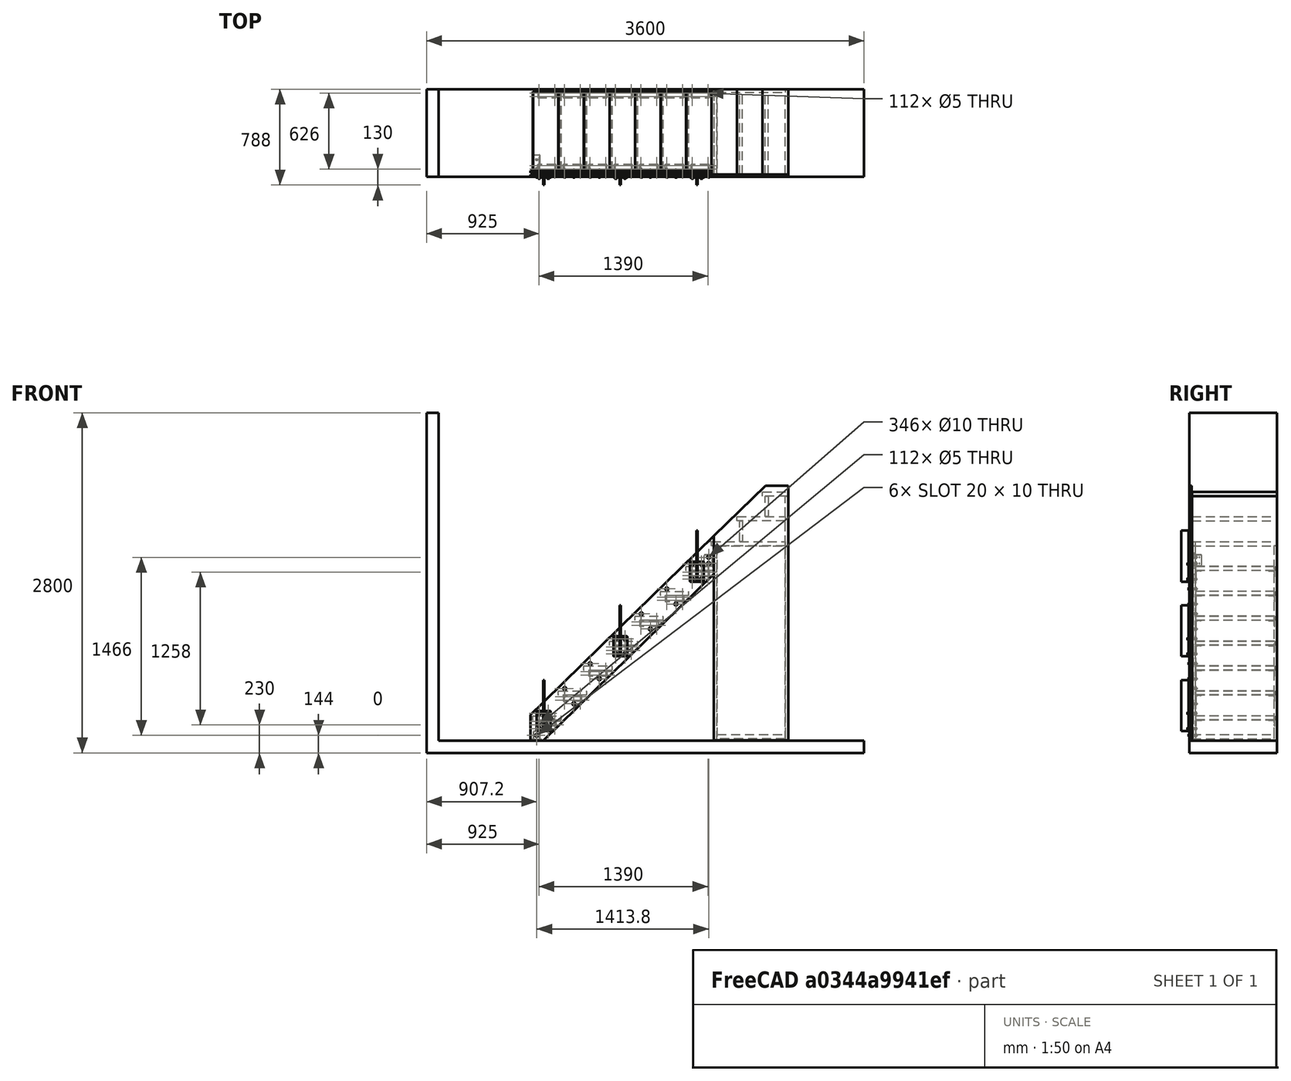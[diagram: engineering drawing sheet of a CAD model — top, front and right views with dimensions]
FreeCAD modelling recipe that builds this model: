
FCSTD DOCUMENT  (FreeCAD 0.17R10980 (Git))
Label: double_beam_board
License: All rights reserved
LicenseURL: http://en.wikipedia.org/wiki/All_rights_reserved
objects: Part::FeaturePython×27, TechDraw::DrawViewDimension×27, Part::Part2DObjectPython×22, TechDraw::DrawViewAnnotation×18, Part::Extrusion×12, Part::Compound×11, Part::Feature×9, TechDraw::DrawViewDetail×7, TechDraw::DrawViewDraft×6, Part::Cut×5, TechDraw::DrawViewPart×3, App::DocumentObjectGroupPython×2, App::DocumentObjectGroup×2, TechDraw::DrawSVGTemplate×1, TechDraw::DrawPage×1
note: 86 computed .brp shape members not serialized (recipe doc carries the construction recipe); baked Part::Feature solids carry a one-line shape summary decoded from their .brp

FEATURE [Part::FeaturePython] beam_01  # a2plus imported part (geometry in sourceFile) (typed FeaturePython)
  fixedPosition = true
  sourceFile = beam.fcstd
  timeLastImport = 1.49397e+09
  updateColors = true
FEATURE [Part::FeaturePython] fridge_box_panels_01  # a2plus imported part (geometry in sourceFile) (typed FeaturePython)
  fixedPosition = false
  sourceFile = A711_fridge_box_panels.fcstd
  timeLastImport = 1.49389e+09
  updateColors = true
FEATURE [Part::Feature] fridge_box_panels_01_cs
  shape: bbox 630 x 3e-07 x 2050 mm, 0 faces, 0 solids (baked)
FEATURE [Part::Part2DObjectPython] DWire  # Draft 2D object (typed FeaturePython)
  ChamferSize = 0
  Closed = true
  End = (1515,-325,1605)
  FilletRadius = 0
  Length = 488.683
  MakeFace = true
  Points = (7) [(1490,-325,1605),(1470,-325,1605),(1470,-325,1640),(1423.45,-325,1640),(1423.45,-325,1757.79),(1515,-325,1757.79),(1515,-325,1605)]
  Start = (1490,-325,1605)
  Subdivisions = 0
  Support = -> [beam_01]
FEATURE [Part::FeaturePython] Clone  label="beam_004"  # Draft clone (typed FeaturePython)
  AttacherType = Attacher::AttachEngine3D
  Objects = -> [beam_01]
  Placement = pos=(0,-30,0) rot=(0,0,1;0rad)
  Scale = (1,1,1)
FEATURE [Part::FeaturePython] stair_profile_01  # a2plus imported part (geometry in sourceFile) (typed FeaturePython)
  fixedPosition = false
  sourceFile = stair_profile.fcstd
  timeLastImport = 1.4938e+09
  updateColors = true
FEATURE [Part::FeaturePython] step_01  # a2plus imported part (geometry in sourceFile) (typed FeaturePython)
  fixedPosition = false
  sourceFile = step.fcstd
  timeLastImport = 1.4938e+09
  updateColors = true
FEATURE [Part::FeaturePython] beam_plate_01  # a2plus imported part (geometry in sourceFile) (typed FeaturePython)
  fixedPosition = false
  sourceFile = beam_plate.fcstd
  timeLastImport = 1.49389e+09
  updateColors = true
FEATURE [Part::Feature] Union
  shape: bbox 26 x 2e-07 x 126 mm, 1 faces, 0 solids (baked)
FEATURE [Part::Feature] Union001
  shape: bbox 86 x 2e-07 x 26 mm, 1 faces, 0 solids (baked)
FEATURE [Part::Part2DObjectPython] Circle001  # Draft 2D object (typed FeaturePython)
  FirstAngle = 0
  LastAngle = 0
  MakeFace = true
  Placement = pos=(32.2,-325,44) rot=(-1,0,0;1.5708rad)
  Radius = 5
FEATURE [Part::Part2DObjectPython] Circle  # Draft 2D object (typed FeaturePython)
  FirstAngle = 0
  LastAngle = 0
  MakeFace = true
  Placement = pos=(1446,-325,1510) rot=(-1,0,0;1.5708rad)
  Radius = 5
FEATURE [Part::Part2DObjectPython] Circle002  # Draft 2D object (typed FeaturePython)
  FirstAngle = 0
  LastAngle = 0
  MakeFace = true
  Placement = pos=(1446,-325,1460) rot=(-1,0,0;1.5708rad)
  Radius = 5
FEATURE [Part::Compound] Compound001
  Links = -> [Union,Union001,DWire]
FEATURE [Part::Compound] Compound002
  Links = -> [Circle001,Circle,Circle002]
FEATURE [Part::Compound] Compound003
  Links = -> [Compound002,Compound001]
FEATURE [Part::Extrusion] Extrude
  Base = -> Compound003
  Dir = (0,-1,0)
  DirMode = 0
  FaceMakerClass = Part::FaceMakerBullseye
  LengthFwd = 20
  LengthRev = 0
  Solid = false
  Symmetric = false
FEATURE [Part::Cut] Cut
  Base = -> beam_01
  Tool = -> Extrude
FEATURE [Part::FeaturePython] Panel001  # WARN: FeaturePython — macro-defined, semantics opaque (R4)
  Area = 0
  Base = -> Cut
  FaceMaker = 0
  HorizontalArea = 0
  Length = 0
  MoveWithHost = false
  Normal = (0,0,0)
  PerimeterLength = 0
  Role = 0
  Sheets = 1
  Thickness = 10
  VerticalArea = 0
  WaveDirection = 0
  WaveHeight = 0
  WaveLength = 0
  WaveType = 0
  Width = 0
FEATURE [Part::Extrusion] Extrude001
  Base = -> Compound002
  Dir = (0,-1,0)
  DirMode = 0
  FaceMakerClass = Part::FaceMakerBullseye
  LengthFwd = 20
  LengthRev = 0
  Placement = pos=(0,-30,0) rot=(0,0,1;0rad)
  Solid = false
  Symmetric = false
FEATURE [Part::Cut] Cut001
  Base = -> Clone
  Tool = -> Extrude001
FEATURE [Part::FeaturePython] Panel  # WARN: FeaturePython — macro-defined, semantics opaque (R4)
  Area = 0
  Base = -> Cut001
  FaceMaker = 0
  HorizontalArea = 0
  Length = 0
  MoveWithHost = false
  Normal = (0,0,0)
  PerimeterLength = 0
  Role = 0
  Sheets = 1
  Thickness = 10
  VerticalArea = 0
  WaveDirection = 0
  WaveHeight = 0
  WaveLength = 0
  WaveType = 0
  Width = 0
FEATURE [Part::Part2DObjectPython] Circle003  # Draft 2D object (typed FeaturePython)
  FirstAngle = 0
  LastAngle = 0
  MakeFace = true
  Placement = pos=(32.2,-375,44) rot=(1,0,0;1.5708rad)
  Radius = 12.5
FEATURE [Part::Extrusion] Extrude002
  Base = -> Circle003
  Dir = (0,-1,0)
  DirMode = 0
  FaceMakerClass = Part::FaceMakerBullseye
  LengthFwd = 2
  LengthRev = 0
  Solid = false
  Symmetric = false
FEATURE [Part::Part2DObjectPython] Circle004  # Draft 2D object (typed FeaturePython)
  FirstAngle = 0
  LastAngle = 0
  MakeFace = true
  Placement = pos=(32.2,-375,44) rot=(1,0,0;1.5708rad)
  Radius = 5
FEATURE [Part::Extrusion] Extrude003
  Base = -> Circle004
  Dir = (0,-1,0)
  DirMode = 0
  FaceMakerClass = Part::FaceMakerBullseye
  LengthFwd = 2
  LengthRev = 0
  Solid = false
  Symmetric = false
FEATURE [Part::Cut] Cut002  label="washer"
  Base = -> Extrude002
  Tool = -> Extrude003
FEATURE [Part::Feature] BOLTS_part011_cs
  Placement = pos=(0,0,-2.5) rot=(0,0,1;0rad)
  shape: bbox 17 x 19.63 x 3e-07 mm, 0 faces, 0 solids (baked)
FEATURE [Part::Extrusion] Extrude004  label="nuts"
  Base = -> BOLTS_part011_cs
  Dir = (0,0,1)
  DirMode = 0
  FaceMakerClass = Part::FaceMakerBullseye
  LengthFwd = 6
  LengthRev = 0
  Placement = pos=(32.2,-347,44) rot=(1,0,0;1.5708rad)
  Solid = true
  Symmetric = false
FEATURE [Part::FeaturePython] Component001  label="washer002"  # WARN: FeaturePython — macro-defined, semantics opaque (R4)
  CloneOf = -> Cut002
  HorizontalArea = 0
  MoveWithHost = false
  PerimeterLength = 0
  Placement = pos=(0,30,0) rot=(0,0,1;0rad)
  Role = 0
  VerticalArea = 0
FEATURE [Part::FeaturePython] Component002  label="washer003"  # WARN: FeaturePython — macro-defined, semantics opaque (R4)
  CloneOf = -> Cut002
  HorizontalArea = 0
  MoveWithHost = false
  PerimeterLength = 0
  Placement = pos=(0,52,0) rot=(0,0,1;0rad)
  Role = 0
  VerticalArea = 0
FEATURE [Part::FeaturePython] Component003  label="nuts001"  # WARN: FeaturePython — macro-defined, semantics opaque (R4)
  CloneOf = -> Extrude004
  HorizontalArea = 0
  MoveWithHost = false
  PerimeterLength = 0
  Placement = pos=(32.2,-317,44) rot=(1,0,0;1.5708rad)
  Role = 0
  VerticalArea = 0
FEATURE [Part::Feature] BOLTS_part  label="Hexagon head bolt DIN 931 M10 - 66.0"
  Placement = pos=(32.2,-383.4,44) rot=(-1,0,0;1.5708rad)
  shape: bbox 17 x 72.4 x 19.63 mm, 11 faces (baked)
FEATURE [TechDraw::DrawSVGTemplate] Template
  EditableTexts = 5cm_scaled_value=50/25/10cm; Architect_2=MARZIA FILATRELLA; Architect_3=MARCO FERRARA; Board_no=A721; Date=5.5.2017; Date_1=5.5.2017; Drawing_title_2=TRAVE PRINCIPALE; Filename=DOUBLE_BEAM.FCSTD; Project_title_2=CASA VACANZE; Project_title_3=A SESTRI; Project_title_4=SCALA INTERNA; Revision=1.0; Scale=VARIE; Sheet_of_sheets=4 DI 7 (nd); Size=A1; Version_1=1.0
  Height = 841
  Orientation = 0
  Width = 594
FEATURE [Part::Feature] step_01_cs  label="hd_steps_cs"
  shape: bbox 1490 x 3e-07 x 1265 mm, 0 faces, 0 solids (baked)
FEATURE [Part::FeaturePython] fridge_box_door_01  # a2plus imported part (geometry in sourceFile) (typed FeaturePython)
  Placement = pos=(0,1e-12,0) rot=(0,0,1;0rad)
  fixedPosition = false
  sourceFile = fridge_box_door.fcstd
  timeLastImport = 1.49385e+09
  updateColors = true
FEATURE [Part::Feature] fridge_box_door_01_cs
  shape: bbox 610 x 3e-07 x 2095 mm, 0 faces, 0 solids (baked)
FEATURE [Part::Part2DObjectPython] DWire003  # Draft 2D object (typed FeaturePython)
  ChamferSize = 0
  Closed = false
  End = (1490,-375,1605)
  FilletRadius = 0
  Length = 55
  MakeFace = true
  Points = (3) [(1470,-375,1640),(1470,-375,1605),(1490,-375,1605)]
  Start = (1470,-375,1640)
  Subdivisions = 0
FEATURE [Part::Part2DObjectPython] Line  # Draft 2D object (typed FeaturePython)
  ChamferSize = 0
  Closed = false
  End = (1490,-375,1640)
  FilletRadius = 0
  Length = 20
  MakeFace = true
  Points = (2) [(1470,-375,1640),(1490,-375,1640)]
  Start = (1470,-375,1640)
  Subdivisions = 0
FEATURE [Part::Part2DObjectPython] Line001  # Draft 2D object (typed FeaturePython)
  ChamferSize = 0
  Closed = false
  End = (1490,-375,0)
  FilletRadius = 0
  Length = 5
  MakeFace = true
  Points = (2) [(1490,-375,5),(1490,-375,0)]
  Start = (1490,-375,5)
  Subdivisions = 0
FEATURE [Part::Part2DObjectPython] Line002  # Draft 2D object (typed FeaturePython)
  ChamferSize = 0
  Closed = false
  End = (2100,-375,0)
  FilletRadius = 0
  Length = 5
  MakeFace = true
  Points = (2) [(2100,-375,5),(2100,-375,2.27374e-13)]
  Start = (2100,-375,5)
  Subdivisions = 0
FEATURE [Part::Part2DObjectPython] DWire001  # Draft 2D object (typed FeaturePython)
  ChamferSize = 0
  Closed = false
  End = (2725,-375,0)
  FilletRadius = 0
  Length = 6200
  MakeFace = true
  Points = (3) [(-775,-375,2700),(-775,-375,-1.13687e-13),(2725,-375,1.00626e-13)]
  Start = (-775,-375,2700)
  Subdivisions = 0
FEATURE [Part::Part2DObjectPython] DWire002  # Draft 2D object (typed FeaturePython)
  ChamferSize = 0
  Closed = false
  End = (2725,-375,2105)
  FilletRadius = 0
  Length = 1405
  MakeFace = true
  Points = (4) [(2725,-375,2260),(2100,-375,2260),(2100,-375,2105),(2725,-375,2105)]
  Start = (2725,-375,2260)
  Subdivisions = 0
FEATURE [Part::Compound] Compound007  label="07_section"
  Links = -> [DWire002,DWire001]
FEATURE [TechDraw::DrawViewDraft] DraftView  label="07_section001"
  Direction = (0,-1,0)
  FontSize = 12
  KeepLabel = false
  LineSpacing = 1
  LineStyle = Solid
  LineWidth = 0.7
  Rotation = -90
  Scale = 0.1
  ScaleType = 2
  Source = -> Compound007
  Symbol = <svg\n xmlns="http://www.w3.org/2000/svg" version="1.1"\n xmlns:freecad="http://www.freecadweb.org/wiki/index.php?title=Svg_Namespace">\n<path id="Compound007_w0000"  d="M -2260.0 -2725.0 L -2260.0 -2100.0 L -2105.0 -2100.0 L -2105.0 -2725.0 " stroke="#000000" stroke-width="7.0 px" style="stroke-width:7.0;stroke-miterlimit:4;stroke-dasharray:none;fill:none;fill-rule: evenodd "/>\n<path id="Compound007_w0001"  d="M -2700.0 775.0 L -5.7e-14 775.0 L -1.01e-13 -2725.0 " stroke="#000000" stroke-width="7.0 px" style="stroke-width:7.0;stroke-miterlimit:4;stroke-dasharray:none;fill:none;fill-rule: evenodd "/>\n\n</svg>
  X = 67.8095
  Y = 363.226
  expr: Y = View.Y + 175.44999999999999
  expr: X = View.X - 136.05000000000001
FEATURE [Part::FeaturePython] Component007  label="07_section002"  # WARN: FeaturePython — macro-defined, semantics opaque (R4)
  CloneOf = -> Compound007
  HorizontalArea = 0
  MoveWithHost = false
  PerimeterLength = 0
  Role = 0
  VerticalArea = 0
FEATURE [Part::FeaturePython] Component008  label="07_section003"  # WARN: FeaturePython — macro-defined, semantics opaque (R4)
  CloneOf = -> Compound007
  HorizontalArea = 0
  MoveWithHost = false
  PerimeterLength = 0
  Role = 0
  VerticalArea = 0
FEATURE [App::DocumentObjectGroupPython] VisGroup001  label="hd_steps"  # scripted group (container) (typed FeaturePython)
  Group = -> [step_01_cs,Component008]
FEATURE [TechDraw::DrawViewDraft] DraftView002  label="hd_steps001"
  Direction = (0,-1,0)
  FontSize = 12
  KeepLabel = false
  LineSpacing = 1
  LineStyle = 3,1
  LineWidth = 0.1
  Rotation = -90
  Scale = 0.1
  ScaleType = 2
  Source = -> VisGroup001
  Symbol = <blob: 2945 chars omitted>
  X = 68.4095
  Y = 363.226
  expr: Y = View.Y + 175.44999999999999
  expr: X = View.X - 135.44999999999999
FEATURE [Part::FeaturePython] Component009  label="07_section004"  # WARN: FeaturePython — macro-defined, semantics opaque (R4)
  CloneOf = -> Compound007
  HorizontalArea = 0
  MoveWithHost = false
  PerimeterLength = 0
  Role = 0
  VerticalArea = 0
FEATURE [Part::FeaturePython] railing_plate_01  # a2plus imported part (geometry in sourceFile) (typed FeaturePython)
  fixedPosition = false
  sourceFile = railing_plate.fcstd
  timeLastImport = 1.49397e+09
  updateColors = true
FEATURE [Part::Compound] Compound010  label="main"
  Links = -> [Panel,Panel001]
FEATURE [Part::Part2DObjectPython] Circle005  # Draft 2D object (typed FeaturePython)
  FirstAngle = 0
  LastAngle = 0
  MakeFace = true
  Placement = pos=(32.2,-375,44) rot=(1,0,0;1.5708rad)
  Radius = 12.5
FEATURE [Part::Extrusion] Extrude007
  Base = -> Circle005
  Dir = (0,-1,0)
  DirMode = 0
  FaceMakerClass = Part::FaceMakerBullseye
  LengthFwd = 2
  LengthRev = 0
  Solid = false
  Symmetric = false
FEATURE [Part::Part2DObjectPython] Circle006  # Draft 2D object (typed FeaturePython)
  FirstAngle = 0
  LastAngle = 0
  MakeFace = true
  Placement = pos=(32.2,-375,44) rot=(1,0,0;1.5708rad)
  Radius = 5
FEATURE [Part::Extrusion] Extrude008
  Base = -> Circle006
  Dir = (0,-1,0)
  DirMode = 0
  FaceMakerClass = Part::FaceMakerBullseye
  LengthFwd = 2
  LengthRev = 0
  Solid = false
  Symmetric = false
FEATURE [Part::Cut] Cut003  label="washer004"
  Base = -> Extrude007
  Placement = pos=(0,-8,0) rot=(0,0,1;0rad)
  Tool = -> Extrude008
FEATURE [Part::Feature] BOLTS_part011_cs001
  Placement = pos=(0,0,-2.5) rot=(0,0,1;0rad)
  shape: bbox 17 x 19.63 x 3e-07 mm, 0 faces, 0 solids (baked)
FEATURE [Part::Extrusion] Extrude009  label="nuts002"
  Base = -> BOLTS_part011_cs001
  Dir = (0,0,1)
  DirMode = 0
  FaceMakerClass = Part::FaceMakerBullseye
  LengthFwd = 6
  LengthRev = 0
  Placement = pos=(32.2,-347,44) rot=(1,0,0;1.5708rad)
  Solid = true
  Symmetric = false
FEATURE [Part::FeaturePython] Component011  label="washer006"  # WARN: FeaturePython — macro-defined, semantics opaque (R4)
  CloneOf = -> Cut003
  HorizontalArea = 0
  MoveWithHost = false
  PerimeterLength = 0
  Placement = pos=(0,30,0) rot=(0,0,1;0rad)
  Role = 0
  VerticalArea = 0
FEATURE [Part::FeaturePython] Component012  label="washer007"  # WARN: FeaturePython — macro-defined, semantics opaque (R4)
  CloneOf = -> Cut003
  HorizontalArea = 0
  MoveWithHost = false
  PerimeterLength = 0
  Placement = pos=(0,52,0) rot=(0,0,1;0rad)
  Role = 0
  VerticalArea = 0
FEATURE [Part::FeaturePython] Component013  label="nuts003"  # WARN: FeaturePython — macro-defined, semantics opaque (R4)
  CloneOf = -> Extrude009
  HorizontalArea = 0
  MoveWithHost = false
  PerimeterLength = 0
  Placement = pos=(32.2,-317,44) rot=(1,0,0;1.5708rad)
  Role = 0
  VerticalArea = 0
FEATURE [Part::Feature] BOLTS_part001  label="Hexagon head bolt DIN 931 M10 - 66.001"
  Placement = pos=(32.2,-391.4,44) rot=(-1,0,0;1.5708rad)
  shape: bbox 17 x 72.4 x 19.63 mm, 11 faces (baked)
FEATURE [Part::Part2DObjectPython] Circle009  # Draft 2D object (typed FeaturePython)
  FirstAngle = 0
  LastAngle = 0
  MakeFace = true
  Placement = pos=(32.2,-355,44) rot=(1,0,0;1.5708rad)
  Radius = 12.5
FEATURE [Part::Extrusion] Extrude013
  Base = -> Circle009
  Dir = (0,1,0)
  DirMode = 0
  FaceMakerClass = Part::FaceMakerBullseye
  LengthFwd = 2
  LengthRev = 0
  Solid = false
  Symmetric = false
FEATURE [Part::Part2DObjectPython] Circle010  # Draft 2D object (typed FeaturePython)
  FirstAngle = 0
  LastAngle = 0
  MakeFace = true
  Placement = pos=(32.2,-355,44) rot=(1,0,0;1.5708rad)
  Radius = 5
FEATURE [Part::Extrusion] Extrude014
  Base = -> Circle010
  Dir = (0,1,0)
  DirMode = 0
  FaceMakerClass = Part::FaceMakerBullseye
  LengthFwd = 2
  LengthRev = 0
  Solid = false
  Symmetric = false
FEATURE [Part::Cut] Cut005  label="washer012"
  Base = -> Extrude013
  Tool = -> Extrude014
FEATURE [Part::Compound] Compound004  label="fastener_and_nuts"
  Links = -> [Cut002,Extrude004,Component003,Component001,Component002,BOLTS_part,Cut005]
FEATURE [Part::FeaturePython] Component005  label="fastener_and_nuts002"  # WARN: FeaturePython — macro-defined, semantics opaque (R4)
  CloneOf = -> Compound004
  HorizontalArea = 0
  MoveWithHost = false
  PerimeterLength = 0
  Placement = pos=(1413.8,0,1466) rot=(0,0,1;0rad)
  Role = 0
  VerticalArea = 0
FEATURE [Part::FeaturePython] Component006  label="fastener_and_nuts003"  # WARN: FeaturePython — macro-defined, semantics opaque (R4)
  CloneOf = -> Compound004
  HorizontalArea = 0
  MoveWithHost = false
  PerimeterLength = 0
  Placement = pos=(1413.8,0,1416) rot=(0,0,1;0rad)
  Role = 0
  VerticalArea = 0
FEATURE [Part::Compound] Compound016  label="fasteners_and_nuts_unique"
  Links = -> [Component005,Compound004,Component006]
FEATURE [Part::FeaturePython] Component  label="washer013"  # WARN: FeaturePython — macro-defined, semantics opaque (R4)
  CloneOf = -> Cut005
  HorizontalArea = 0
  MoveWithHost = false
  PerimeterLength = 0
  Role = 0
  VerticalArea = 0
FEATURE [Part::Compound] Compound013  label="fastener_and_nuts_railing"
  Links = -> [Cut003,Extrude009,Component013,Component011,Component012,BOLTS_part001,Component]
  Placement = pos=(19.6902,0,56) rot=(0,0,1;0rad)
FEATURE [Part::FeaturePython] Component018  label="fastener_and_nuts006"  # WARN: FeaturePython — macro-defined, semantics opaque (R4)
  CloneOf = -> Compound004
  HorizontalArea = 0
  MoveWithHost = false
  PerimeterLength = 0
  Placement = pos=(229.7,0,386) rot=(0,0,1;0rad)
  Role = 0
  VerticalArea = 0
FEATURE [Part::FeaturePython] Array001  # Draft array (typed FeaturePython)
  Angle = 360
  ArrayType = 0
  Axis = (0,0,1)
  Base = -> Component018
  Center = (0,0,0)
  Fuse = false
  IntervalAxis = (0,0,0)
  IntervalX = (75,0,-125)
  IntervalY = (0,0,125)
  IntervalZ = (210,0,205)
  NumberPolar = 1
  NumberX = 2
  NumberY = 1
  NumberZ = 2
FEATURE [Part::FeaturePython] Array002  label="fasteners"  # Draft array (typed FeaturePython)
  Angle = 360
  ArrayType = 0
  Axis = (0,0,1)
  Base = -> Array001
  Center = (0,0,0)
  Fuse = false
  IntervalAxis = (0,0,0)
  IntervalX = (630,0,615)
  IntervalY = (0,1,0)
  IntervalZ = (0,0,0)
  NumberPolar = 1
  NumberX = 2
  NumberY = 1
  NumberZ = 1
FEATURE [Part::FeaturePython] Array  label="fasteners_railing"  # Draft array (typed FeaturePython)
  Angle = 360
  ArrayType = 0
  Axis = (0,0,1)
  Base = -> Compound013
  Center = (0,0,0)
  Fuse = false
  IntervalAxis = (0,0,0)
  IntervalX = (75,0,0)
  IntervalY = (0,0,125)
  IntervalZ = (630,0,615)
  NumberPolar = 1
  NumberX = 2
  NumberY = 2
  NumberZ = 3
FEATURE [Part::Part2DObjectPython] Rectangle  label="gr_detail001"  # Draft 2D object (typed FeaturePython)
  ChamferSize = 0
  Columns = 1
  FilletRadius = 10
  Height = 100
  Length = 100
  MakeFace = false
  Placement = pos=(216.28,-119.156,0) rot=(0,0,1;0rad)
  Rows = 1
FEATURE [TechDraw::DrawViewDraft] DraftView003  label="gr_detailA"
  Direction = (0,0,-1)
  FontSize = 12
  KeepLabel = false
  LineSpacing = 1
  LineStyle = 6,3,.7,3
  LineWidth = 1
  Rotation = 0
  Scale = 0.45
  ScaleType = 2
  Source = -> Rectangle
  Symbol = <svg\n xmlns="http://www.w3.org/2000/svg" version="1.1"\n xmlns:freecad="http://www.freecadweb.org/wiki/index.php?title=Svg_Namespace">\n<path id="Rectangle_w0000"  d="M -226.279953003 119.156494141 L -306.279953003 119.156494141 M -306.279953003 119.156494141 L -316.279953003 109.156494141 L -316.279953003 29.156494141 M -316.279953003 29.156494141 L -306.279953003 19.156494141 L -226.279953003 19.156494141 M -226.279953003 19.156494141 L -216.279953003 29.156494141 L -216.279953003 109.156494141 M -216.279953003 109.156494141 L -226.279953003 119.156494141 " stroke="#000000" stroke-width="2.22222222222 px" style="stroke-width:2.22222222222;stroke-miterlimit:4;stroke-dasharray:13.3333333333,6.66666666667,1.55555555556,6.66666666667;fill:none;fill-rule: evenodd "/>\n\n</svg>
  X = 88.8595
  Y = 87.7759
  expr: Y = front_view.Y - 100
  expr: X = front_view.X - 115
FEATURE [Part::Part2DObjectPython] Rectangle001  # Draft 2D object (typed FeaturePython)
  ChamferSize = 0
  Columns = 1
  FilletRadius = 0
  Height = 1605
  Length = 700
  MakeFace = true
  Placement = pos=(1490,345,0) rot=(0.57735,-0.57735,-0.57735;2.0944rad)
  Rows = 1
  Support = -> [fridge_box_panels_01]
FEATURE [Part::Extrusion] Extrude015  label="fridge_box_side"
  Base = -> Rectangle001
  Dir = (1,0,0)
  DirMode = 0
  FaceMakerClass = Part::FaceMakerBullseye
  LengthFwd = 25
  LengthRev = 0
  Solid = false
  Symmetric = false
FEATURE [Part::Compound] Compound015  label="plan_detail"
  Links = -> [Panel,Panel001,railing_plate_01,beam_plate_01,Array002,Array,Compound016,Extrude015,fridge_box_door_01]
FEATURE [TechDraw::DrawViewPart] View001  label="plan_view"
  ArcCenterMarks = true
  CenterScale = 2
  Direction = (0,0,1)
  HardHidden = false
  HiddenWidth = 0.15
  HorizCenterLine = false
  IsoCount = 0
  IsoHidden = false
  IsoVisible = false
  IsoWidth = 0.3
  KeepLabel = false
  LineWidth = 0.25
  Rotation = 0
  Scale = 0.1
  ScaleType = 2
  SeamHidden = false
  SeamVisible = false
  ShowSectionLine = true
  SmoothHidden = false
  SmoothVisible = false
  Source = -> Compound015
  VertCenterLine = false
  X = -155.002
  Y = 490.968
FEATURE [TechDraw::DrawViewDetail] Detail003  label="DetailA_plan"
  AnchorPoint = (-980,-280,0)
  ArcCenterMarks = true
  BaseView = -> View001
  CenterScale = 2
  Direction = (0,0,1)
  HardHidden = true
  HiddenWidth = 0.15
  HorizCenterLine = false
  IsoCount = 0
  IsoHidden = false
  IsoVisible = false
  IsoWidth = 0.3
  KeepLabel = false
  LineWidth = 0.25
  Radius = 250
  Reference = 1
  Rotation = 0
  Scale = 0.5
  ScaleType = 2
  SeamHidden = false
  SeamVisible = false
  ShowSectionLine = true
  SmoothHidden = false
  SmoothVisible = false
  Source = -> Compound015
  VertCenterLine = false
  X = 166.527
  Y = 442.97
FEATURE [TechDraw::DrawViewDetail] Detail004  label="DetailC_plan"
  AnchorPoint = (375,-280,0)
  ArcCenterMarks = true
  BaseView = -> View001
  CenterScale = 2
  Direction = (0,0,1)
  HardHidden = true
  HiddenWidth = 0.15
  HorizCenterLine = false
  IsoCount = 0
  IsoHidden = false
  IsoVisible = false
  IsoWidth = 0.3
  KeepLabel = false
  LineWidth = 0.25
  Radius = 250
  Reference = 1
  Rotation = 0
  Scale = 0.5
  ScaleType = 2
  SeamHidden = false
  SeamVisible = false
  ShowSectionLine = true
  SmoothHidden = false
  SmoothVisible = false
  Source = -> Compound015
  VertCenterLine = false
  X = 166.527
  Y = 680.166
  expr: X = DetailA_plan.X
FEATURE [TechDraw::DrawViewDraft] DraftView004  label="gr_detailB"
  Direction = (0,0,-1)
  FontSize = 12
  KeepLabel = false
  LineSpacing = 1
  LineStyle = 6,3,.7,3
  LineWidth = 1
  Rotation = 0
  Scale = 0.5
  ScaleType = 2
  Source = -> Rectangle
  Symbol = <svg\n xmlns="http://www.w3.org/2000/svg" version="1.1"\n xmlns:freecad="http://www.freecadweb.org/wiki/index.php?title=Svg_Namespace">\n<path id="Rectangle_w0000"  d="M -226.279953003 119.156494141 L -306.279953003 119.156494141 M -306.279953003 119.156494141 L -316.279953003 109.156494141 L -316.279953003 29.156494141 M -316.279953003 29.156494141 L -306.279953003 19.156494141 L -226.279953003 19.156494141 M -226.279953003 19.156494141 L -216.279953003 29.156494141 L -216.279953003 109.156494141 M -216.279953003 109.156494141 L -226.279953003 119.156494141 " stroke="#000000" stroke-width="2.0 px" style="stroke-width:2.0;stroke-miterlimit:4;stroke-dasharray:12.0,6.0,1.4,6.0;fill:none;fill-rule: evenodd "/>\n\n</svg>
  X = 162.859
  Y = 165.776
  expr: Y = View.Y - 22
  expr: X = View.X - 41
FEATURE [TechDraw::DrawViewDraft] DraftView005  label="gr_detailC"
  Direction = (0,0,-1)
  FontSize = 12
  KeepLabel = false
  LineSpacing = 1
  LineStyle = 6,3,.7,3
  LineWidth = 1
  Rotation = 0
  Scale = 0.5
  ScaleType = 2
  Source = -> Rectangle
  Symbol = <svg\n xmlns="http://www.w3.org/2000/svg" version="1.1"\n xmlns:freecad="http://www.freecadweb.org/wiki/index.php?title=Svg_Namespace">\n<path id="Rectangle_w0000"  d="M -226.279953003 119.156494141 L -306.279953003 119.156494141 M -306.279953003 119.156494141 L -316.279953003 109.156494141 L -316.279953003 29.156494141 M -316.279953003 29.156494141 L -306.279953003 19.156494141 L -226.279953003 19.156494141 M -226.279953003 19.156494141 L -216.279953003 29.156494141 L -216.279953003 109.156494141 M -216.279953003 109.156494141 L -226.279953003 119.156494141 " stroke="#000000" stroke-width="2.0 px" style="stroke-width:2.0;stroke-miterlimit:4;stroke-dasharray:12.0,6.0,1.4,6.0;fill:none;fill-rule: evenodd "/>\n\n</svg>
  X = 217.259
  Y = 226.776
  expr: Y = View.Y + 39
  expr: X = View.X + 13.4
FEATURE [Part::Part2DObjectPython] Shape2DView  label="dr_railing_plate"  # Draft 2D object (typed FeaturePython)
  Base = -> railing_plate_01
  HiddenLines = false
  InPlace = true
  Placement = pos=(0,-375,2.64049e-05) rot=(0.57735,0.57735,-0.57735;2.0944rad)
  Projection = (0,-1,5.9605e-08)
  ProjectionMode = 0
  SegmentLength = 0.05
  Tessellation = false
FEATURE [TechDraw::DrawViewPart] View002  label="axo"
  ArcCenterMarks = true
  CenterScale = 2
  Direction = (-1,1,1)
  HardHidden = true
  HiddenWidth = 0.15
  HorizCenterLine = false
  IsoCount = 0
  IsoHidden = false
  IsoVisible = false
  IsoWidth = 0.3
  KeepLabel = false
  LineWidth = 0.25
  Rotation = 0
  Scale = 0.1
  ScaleType = 2
  SeamHidden = false
  SeamVisible = false
  ShowSectionLine = true
  SmoothHidden = false
  SmoothVisible = false
  Source = -> Compound010
  VertCenterLine = false
  X = -127.92
  Y = 310.072
FEATURE [TechDraw::DrawViewDetail] Detail005  label="DetailA_axo"
  AnchorPoint = (1050,-900,0)
  ArcCenterMarks = true
  BaseView = -> View002
  CenterScale = 2
  Direction = (-1,1,1)
  HardHidden = true
  HiddenWidth = 0.15
  HorizCenterLine = false
  IsoCount = 0
  IsoHidden = false
  IsoVisible = false
  IsoWidth = 0.3
  KeepLabel = false
  LineWidth = 0.25
  Radius = 300
  Reference = 1
  Rotation = 0
  Scale = 0.35
  ScaleType = 2
  SeamHidden = false
  SeamVisible = false
  ShowSectionLine = true
  SmoothHidden = false
  SmoothVisible = false
  Source = -> Compound015
  VertCenterLine = false
  X = 454.166
  Y = 496.192
FEATURE [TechDraw::DrawViewDetail] Detail006  label="DetailC_axo"
  AnchorPoint = (100,800,0)
  ArcCenterMarks = true
  BaseView = -> View002
  CenterScale = 2
  Direction = (-1,1,1)
  HardHidden = true
  HiddenWidth = 0.15
  HorizCenterLine = false
  IsoCount = 0
  IsoHidden = false
  IsoVisible = false
  IsoWidth = 0.3
  KeepLabel = false
  LineWidth = 0.25
  Radius = 300
  Reference = 1
  Rotation = 0
  Scale = 0.35
  ScaleType = 2
  SeamHidden = false
  SeamVisible = false
  ShowSectionLine = true
  SmoothHidden = false
  SmoothVisible = false
  Source = -> Compound015
  VertCenterLine = false
  X = 454.166
  Y = 697.104
  expr: X = DetailA_axo.X
FEATURE [TechDraw::DrawViewAnnotation] Annotation  label="vista_frontale"
  Font = Arial
  KeepLabel = false
  LineSpace = 100
  MaxWidth = -1
  Rotation = 0
  ScaleType = 0
  Text = VISTA FRONTALE | scala 1:10
  TextSize = 3
  TextStyle = 1
  X = 28.6386
  Y = 47.7594
FEATURE [TechDraw::DrawViewAnnotation] Annotation001  label="A"
  Font = Arial
  KeepLabel = false
  LineSpace = 80
  MaxWidth = -1
  Rotation = 0
  ScaleType = 0
  Text = A
  TextSize = 5
  TextStyle = 1
  X = 92.4109
  Y = 83.4178
FEATURE [TechDraw::DrawViewAnnotation] Annotation002  label="B"
  Font = Arial
  KeepLabel = false
  LineSpace = 80
  MaxWidth = -1
  Rotation = 0
  ScaleType = 0
  Text = B
  TextSize = 5
  TextStyle = 1
  X = 167.021
  Y = 162.553
FEATURE [TechDraw::DrawViewAnnotation] Annotation003  label="C"
  Font = Arial
  KeepLabel = false
  LineSpace = 80
  MaxWidth = -1
  Rotation = 0
  ScaleType = 0
  Text = C
  TextSize = 5
  TextStyle = 1
  X = 221.322
  Y = 223.517
FEATURE [TechDraw::DrawViewAnnotation] Annotation004  label="dettaglio_A"
  Font = Arial
  KeepLabel = false
  LineSpace = 100
  MaxWidth = -1
  Rotation = 0
  ScaleType = 0
  Text = DETTAGLIO A |  vista frontale scala 1:5
  TextSize = 3
  TextStyle = 1
  X = 414.908
  Y = 37.4778
  expr: Y = DetailA.Y - 45
  expr: X = DetailA.X - 43
FEATURE [TechDraw::DrawViewAnnotation] Annotation005  label="dettaglio_B"
  Font = Arial
  KeepLabel = false
  LineSpace = 100
  MaxWidth = -1
  Rotation = 0
  ScaleType = 0
  Text = DETTAGLIO B |  vista frontale scala 1:5
  TextSize = 3
  TextStyle = 1
  X = 414.908
  Y = 153.78
  expr: Y = DetailB.Y - 45
  expr: X = DetailB.X - 43
FEATURE [TechDraw::DrawViewAnnotation] Annotation006  label="dettaglio_C"
  Font = Arial
  KeepLabel = false
  LineSpace = 100
  MaxWidth = -1
  Rotation = 0
  ScaleType = 0
  Text = DETTAGLIO C |  vista frontale scala 1:5
  TextSize = 3
  TextStyle = 1
  X = 414.908
  Y = 270.082
  expr: Y = DetailC.Y - 45
  expr: X = DetailC.X - 43
FEATURE [TechDraw::DrawViewAnnotation] Annotation007  label="dettaglio_A_plan"
  Font = Arial
  KeepLabel = false
  LineSpace = 100
  MaxWidth = -1
  Rotation = 0
  ScaleType = 0
  Text = DETTAGLIO A |  pianta scala 1:2
  TextSize = 3
  TextStyle = 1
  X = 78.0268
  Y = 351.67
  expr: Y = DetailA_plan.Y - 91.299999999999997
  expr: X = DetailA_plan.X - 88.5
FEATURE [TechDraw::DrawViewAnnotation] Annotation008  label="dettaglio_C_plan"
  Font = Arial
  KeepLabel = false
  LineSpace = 100
  MaxWidth = -1
  Rotation = 0
  ScaleType = 0
  Text = DETTAGLIO C |  pianta scala 1:2
  TextSize = 3
  TextStyle = 1
  X = 78.0268
  Y = 588.866
  expr: Y = DetailC_plan.Y - 91.299999999999997
  expr: X = DetailC_plan.X - 88.5
FEATURE [TechDraw::DrawViewAnnotation] Annotation009  label="dettaglio_A_axo"
  Font = Arial
  KeepLabel = false
  LineSpace = 100
  MaxWidth = -1
  Rotation = 0
  ScaleType = 0
  Text = DETTAGLIO A | vista assonometrica
  TextSize = 3
  TextStyle = 1
  X = 379.866
  Y = 418.692
  expr: Y = DetailA_axo.Y - 77.5
  expr: X = DetailA_axo.X - 74.299999999999997
FEATURE [TechDraw::DrawViewAnnotation] Annotation010  label="dettaglio_C_axo"
  Font = Arial
  KeepLabel = false
  LineSpace = 100
  MaxWidth = -1
  Rotation = 0
  ScaleType = 0
  Text = DETTAGLIO C | vista assonometrica
  TextSize = 3
  TextStyle = 1
  X = 379.866
  Y = 619.604
  expr: Y = DetailC_axo.Y - 77.5
  expr: X = DetailC_axo.X - 74.299999999999997
FEATURE [TechDraw::DrawViewDimension] Dimension025
  Font = Arial
  Fontsize = 3
  FormatSpec = %value%
  KeepLabel = false
  LineWidth = 0.1
  MeasureType = 1
  References2D = -> [Detail003]
  Rotation = 0
  ScaleType = 0
  Type = 2
  X = -50.2948
  Y = 3.01167
FEATURE [TechDraw::DrawViewDimension] Dimension026
  Font = Arial
  Fontsize = 3
  FormatSpec = %value%
  KeepLabel = false
  LineWidth = 0.1
  MeasureType = 1
  References2D = -> [Detail003]
  Rotation = 0
  ScaleType = 0
  Type = 2
  X = -49.4415
  Y = 15.8113
FEATURE [TechDraw::DrawViewDimension] Dimension027
  Font = Arial
  Fontsize = 3
  FormatSpec = %value%
  KeepLabel = false
  LineWidth = 0.1
  MeasureType = 1
  References2D = -> [Detail003]
  Rotation = 0
  ScaleType = 0
  Type = 2
  X = -58.7275
  Y = 10.2899
FEATURE [TechDraw::DrawViewDimension] Dimension028
  Font = Arial
  Fontsize = 3
  FormatSpec = Distanziatore da 1cm
  KeepLabel = false
  LineWidth = 0.1
  MeasureType = 1
  References2D = -> [Detail003]
  Rotation = 0
  ScaleType = 0
  Type = 2
  X = 44.5465
  Y = -27.1287
FEATURE [Part::FeaturePython] plate_01  # a2plus imported part (geometry in sourceFile) (typed FeaturePython)
  fixedPosition = false
  sourceFile = plate.fcstd
  timeLastImport = 1.49399e+09
  updateColors = true
FEATURE [Part::Compound] Compound  label="main_view"
  Links = -> [Panel,Panel001,Component009,plate_01]
FEATURE [App::DocumentObjectGroup] Group  label="utilities"
  Group = -> [step_01,stair_profile_01,fridge_box_panels_01_cs,fridge_box_panels_01,beam_plate_01,fridge_box_door_01,plate_01]
FEATURE [TechDraw::DrawViewPart] View  label="front_view"
  ArcCenterMarks = true
  CenterScale = 2.5
  Direction = (0,-1,0)
  HardHidden = true
  HiddenWidth = 0.1
  HorizCenterLine = false
  IsoCount = 0
  IsoHidden = false
  IsoVisible = false
  IsoWidth = 0.3
  KeepLabel = false
  LineWidth = 0.25
  Rotation = 0
  Scale = 0.1
  ScaleType = 2
  SeamHidden = false
  SeamVisible = false
  ShowSectionLine = true
  SmoothHidden = false
  SmoothVisible = false
  Source = -> Compound
  VertCenterLine = false
  X = 203.859
  Y = 187.776
FEATURE [Part::Part2DObjectPython] DWire004  # Draft 2D object (typed FeaturePython)
  ChamferSize = 0
  Closed = true
  End = (-875,-375,2700)
  FilletRadius = 0
  Length = 12800
  MakeFace = true
  Points = (6) [(-775,-375,2700),(-775,-375,-2.27374e-13),(2725,-375,2.27374e-13),(2725,-375,-100),(-875,-375,-100),(-875,-375,2700)]
  Start = (-775,-375,2700)
  Subdivisions = 0
  Support = -> [Compound]
FEATURE [Part::Extrusion] Extrude006  label="floor"
  Base = -> DWire004
  Dir = (0,1,0)
  DirMode = 0
  FaceMakerClass = Part::FaceMakerBullseye
  LengthFwd = 720
  LengthRev = 0
  Solid = false
  Symmetric = false
FEATURE [Part::Compound] Compound008  label="details"
  Links = -> [Panel,Panel001,fridge_box_panels_01,beam_plate_01,Extrude006,step_01,fridge_box_door_01,railing_plate_01,plate_01]
FEATURE [TechDraw::DrawViewDetail] Detail  label="DetailA"
  AnchorPoint = (-900,-1150,0)
  ArcCenterMarks = true
  BaseView = -> View
  CenterScale = 2.5
  Direction = (0,-1,0)
  HardHidden = true
  HiddenWidth = 0.15
  HorizCenterLine = false
  IsoCount = 0
  IsoHidden = false
  IsoVisible = false
  IsoWidth = 0.3
  KeepLabel = false
  LineWidth = 0.25
  Radius = 300
  Reference = 1
  Rotation = 0
  Scale = 0.2
  ScaleType = 2
  SeamHidden = false
  SeamVisible = false
  ShowSectionLine = true
  SmoothHidden = false
  SmoothVisible = false
  Source = -> Compound008
  VertCenterLine = false
  X = 457.908
  Y = 82.4778
  expr: AnchorPoint.y = 250 - Compound008.Shape.BoundBox.ZLength / 2
  expr: AnchorPoint.x = 900 - Compound008.Shape.BoundBox.XLength / 2
FEATURE [TechDraw::DrawViewDetail] Detail001  label="DetailC"
  AnchorPoint = (500,200,0)
  ArcCenterMarks = true
  BaseView = -> View
  CenterScale = 2.5
  Direction = (0,-1,0)
  HardHidden = true
  HiddenWidth = 0.15
  HorizCenterLine = false
  IsoCount = 0
  IsoHidden = false
  IsoVisible = false
  IsoWidth = 0.3
  KeepLabel = false
  LineWidth = 0.25
  Radius = 300
  Reference = 1
  Rotation = 0
  Scale = 0.2
  ScaleType = 2
  SeamHidden = false
  SeamVisible = false
  ShowSectionLine = true
  SmoothHidden = false
  SmoothVisible = false
  Source = -> Compound008
  VertCenterLine = false
  X = 457.908
  Y = 315.082
  expr: X = DetailA.X
  expr: AnchorPoint.y = 1600 - Compound008.Shape.BoundBox.ZLength / 2
  expr: AnchorPoint.x = 2300 - Compound008.Shape.BoundBox.XLength / 2
FEATURE [TechDraw::DrawViewDetail] Detail002  label="DetailB"
  AnchorPoint = (-100,-425,0)
  ArcCenterMarks = true
  BaseView = -> View
  CenterScale = 2.5
  Direction = (0,-1,0)
  HardHidden = true
  HiddenWidth = 0.15
  HorizCenterLine = false
  IsoCount = 0
  IsoHidden = false
  IsoVisible = false
  IsoWidth = 0.3
  KeepLabel = false
  LineWidth = 0.25
  Radius = 300
  Reference = 1
  Rotation = 0
  Scale = 0.2
  ScaleType = 2
  SeamHidden = false
  SeamVisible = false
  ShowSectionLine = true
  SmoothHidden = false
  SmoothVisible = false
  Source = -> Compound008
  VertCenterLine = false
  X = 457.908
  Y = 198.78
  expr: AnchorPoint.y = 50 + Detail.AnchorPoint.y + (Detail001.AnchorPoint.y - Detail.AnchorPoint.y) / 2
  expr: AnchorPoint.x = 100 + Detail.AnchorPoint.x + (Detail001.AnchorPoint.x - Detail.AnchorPoint.x) / 2
  expr: X = Detail.X
  expr: Y = Detail.Y + (Detail001.Y - Detail.Y) / 2
FEATURE [TechDraw::DrawViewDimension] Dimension
  Font = Arial
  Fontsize = 3
  FormatSpec = %value%
  KeepLabel = false
  LineWidth = 0.1
  MeasureType = 1
  References2D = -> [View]
  Rotation = 0
  ScaleType = 0
  Type = 1
  X = -29.5609
  Y = 154.149
FEATURE [TechDraw::DrawViewDimension] Dimension001
  Font = Arial
  Fontsize = 3
  FormatSpec = %value%
  KeepLabel = false
  LineWidth = 0.1
  MeasureType = 1
  References2D = -> [View]
  Rotation = 0
  ScaleType = 0
  Type = 2
  X = 67.4529
  Y = 30.762
FEATURE [TechDraw::DrawViewDimension] Dimension002
  Font = Arial
  Fontsize = 3
  FormatSpec = %value%
  KeepLabel = false
  LineWidth = 0.1
  MeasureType = 1
  References2D = -> [View]
  Rotation = 0
  ScaleType = 0
  Type = 0
  X = -56.5427
  Y = 88.758
FEATURE [TechDraw::DrawViewDimension] Dimension003
  Font = Arial
  Fontsize = 3
  FormatSpec = %value%
  KeepLabel = false
  LineWidth = 0.1
  MeasureType = 1
  References2D = -> [View]
  Rotation = 0
  ScaleType = 0
  Type = 0
  X = -52.3631
  Y = 57.1395
FEATURE [TechDraw::DrawViewDimension] Dimension004
  Font = Arial
  Fontsize = 3
  FormatSpec = %value%
  KeepLabel = false
  LineWidth = 0.1
  MeasureType = 1
  References2D = -> [View]
  Rotation = 0
  ScaleType = 0
  Type = 0
  X = -26.6032
  Y = 84.8777
FEATURE [TechDraw::DrawViewDimension] Dimension005
  Font = Arial
  Fontsize = 3
  FormatSpec = %value%
  KeepLabel = false
  LineWidth = 0.1
  MeasureType = 1
  References2D = -> [View]
  Rotation = 0
  ScaleType = 0
  Type = 2
  X = 56.7794
  Y = -18.033
FEATURE [TechDraw::DrawViewDimension] Dimension006
  Font = Arial
  Fontsize = 3
  FormatSpec = %value%
  KeepLabel = false
  LineWidth = 0.1
  MeasureType = 1
  References2D = -> [View]
  Rotation = 0
  ScaleType = 0
  Type = 1
  X = -106.571
  Y = 139.599
FEATURE [TechDraw::DrawViewDimension] Dimension007
  Font = Arial
  Fontsize = 3
  FormatSpec = %value%
  KeepLabel = false
  LineWidth = 0.1
  MeasureType = 1
  References2D = -> [View]
  Rotation = 0
  ScaleType = 0
  Type = 2
  X = -108.326
  Y = 123.557
FEATURE [TechDraw::DrawViewDimension] Dimension008
  Font = Arial
  Fontsize = 3
  FormatSpec = %value%
  KeepLabel = false
  LineWidth = 0.1
  MeasureType = 1
  References2D = -> [Detail]
  Rotation = 0
  ScaleType = 0
  Type = 2
  X = -20.5658
  Y = 7.14574
FEATURE [TechDraw::DrawViewDimension] Dimension009
  Font = Arial
  Fontsize = 3
  FormatSpec = %value%
  KeepLabel = false
  LineWidth = 0.1
  MeasureType = 1
  References2D = -> [Detail]
  Rotation = 0
  ScaleType = 0
  Type = 1
  X = 1.39429
  Y = 34.1601
FEATURE [TechDraw::DrawViewDimension] Dimension012
  Font = Arial
  Fontsize = 3
  FormatSpec = %value%
  KeepLabel = false
  LineWidth = 0.1
  MeasureType = 1
  References2D = -> [Detail]
  Rotation = 0
  ScaleType = 0
  Type = 1
  X = -14.8143
  Y = -18.8229
FEATURE [TechDraw::DrawViewDimension] Dimension013
  Font = Arial
  Fontsize = 3
  FormatSpec = %value%
  KeepLabel = false
  LineWidth = 0.1
  MeasureType = 1
  References2D = -> [Detail]
  Rotation = 0
  ScaleType = 0
  Type = 2
  X = 29.6067
  Y = -3.10529
FEATURE [TechDraw::DrawViewDimension] Dimension014
  Font = Arial
  Fontsize = 3
  FormatSpec = %value%
  KeepLabel = false
  LineWidth = 0.1
  MeasureType = 1
  References2D = -> [Detail]
  Rotation = 0
  ScaleType = 0
  Type = 1
  X = 12.6289
  Y = 16.3443
FEATURE [TechDraw::DrawViewDimension] Dimension015
  Font = Arial
  Fontsize = 3
  FormatSpec = %value%
  KeepLabel = false
  LineWidth = 0.1
  MeasureType = 1
  References2D = -> [Detail002]
  Rotation = 0
  ScaleType = 0
  Type = 2
  X = -5.15487
  Y = -0.381842
FEATURE [TechDraw::DrawViewDimension] Dimension016
  Font = Arial
  Fontsize = 3
  FormatSpec = %value%
  KeepLabel = false
  LineWidth = 0.1
  MeasureType = 1
  References2D = -> [Detail002]
  Rotation = 0
  ScaleType = 0
  Type = 1
  X = -21.1922
  Y = 38.1842
FEATURE [TechDraw::DrawViewDimension] Dimension017
  Font = Arial
  Fontsize = 3
  FormatSpec = %value%
  KeepLabel = false
  LineWidth = 0.1
  MeasureType = 1
  References2D = -> [Detail002]
  Rotation = 0
  ScaleType = 0
  Type = 1
  X = -32.6475
  Y = 38.1842
FEATURE [TechDraw::DrawViewDimension] Dimension018
  Font = Arial
  Fontsize = 3
  FormatSpec = %value%
  KeepLabel = false
  LineWidth = 0.1
  MeasureType = 1
  References2D = -> [Detail002]
  Rotation = 0
  ScaleType = 0
  Type = 1
  X = 0
  Y = 38.1842
FEATURE [TechDraw::DrawViewDimension] Dimension019
  Font = Arial
  Fontsize = 3
  FormatSpec = %value%
  KeepLabel = false
  LineWidth = 0.1
  MeasureType = 1
  References2D = -> [Detail002]
  Rotation = 0
  ScaleType = 0
  Type = 2
  X = -37.0705
  Y = 20.2058
FEATURE [TechDraw::DrawViewDimension] Dimension020
  Font = Arial
  Fontsize = 3
  FormatSpec = %value%
  KeepLabel = false
  LineWidth = 0.1
  MeasureType = 1
  References2D = -> [Detail002]
  Rotation = 0
  ScaleType = 0
  Type = 1
  X = -6.27431
  Y = -39.563
FEATURE [TechDraw::DrawViewDimension] Dimension021
  Font = Arial
  Fontsize = 3
  FormatSpec = %value%
  KeepLabel = false
  LineWidth = 0.1
  MeasureType = 1
  References2D = -> [Detail002]
  Rotation = 0
  ScaleType = 0
  Type = 2
  X = -37.2973
  Y = -16.5572
FEATURE [TechDraw::DrawViewDimension] Dimension022
  Font = Arial
  Fontsize = 3
  FormatSpec = %value%
  KeepLabel = false
  LineWidth = 0.1
  MeasureType = 1
  References2D = -> [Detail002]
  Rotation = 0
  ScaleType = 0
  Type = 1
  X = 21.6115
  Y = -39.7373
FEATURE [TechDraw::DrawViewDimension] Dimension023
  Font = Arial
  Fontsize = 3
  FormatSpec = %value%
  KeepLabel = false
  LineWidth = 0.1
  MeasureType = 1
  References2D = -> [Detail002]
  Rotation = 0
  ScaleType = 0
  Type = 2
  X = 32.9401
  Y = -20.5658
FEATURE [TechDraw::DrawViewDimension] Dimension024
  Font = Arial
  Fontsize = 3
  FormatSpec = %value%
  KeepLabel = false
  LineWidth = 0.1
  MeasureType = 1
  References2D = -> [Detail001]
  Rotation = 0
  ScaleType = 0
  Type = 2
  X = 23.3687
  Y = -5.95674
FEATURE [TechDraw::DrawViewAnnotation] Annotation011  label="1_plan"
  Font = Arial
  KeepLabel = false
  LineSpace = 100
  MaxWidth = -1
  Rotation = 0
  ScaleType = 0
  Text = 1
  TextSize = 5
  TextStyle = 3
  X = 149.464
  Y = 480.53
FEATURE [TechDraw::DrawViewAnnotation] Annotation012  label="1_axo"
  Font = Arial
  KeepLabel = false
  LineSpace = 100
  MaxWidth = -1
  Rotation = 0
  ScaleType = 0
  Text = 1
  TextSize = 5
  TextStyle = 3
  X = 453.802
  Y = 452.839
FEATURE [TechDraw::DrawViewAnnotation] Annotation013  label="2_plan"
  Font = Arial
  KeepLabel = false
  LineSpace = 100
  MaxWidth = -1
  Rotation = 0
  ScaleType = 0
  Text = 2
  TextSize = 5
  TextStyle = 3
  X = 193.043
  Y = 700.87
FEATURE [TechDraw::DrawViewAnnotation] Annotation014  label="2_axo"
  Font = Arial
  KeepLabel = false
  LineSpace = 100
  MaxWidth = -1
  Rotation = 0
  ScaleType = 0
  Text = 2
  TextSize = 5
  TextStyle = 3
  X = 436.267
  Y = 693.384
FEATURE [TechDraw::DrawViewAnnotation] Annotation015  label="plate_anno"
  Font = Arial
  KeepLabel = false
  LineSpace = 100
  MaxWidth = -1
  Rotation = 0
  ScaleType = 0
  Text = La forma e le dimensioni delle piastre | 1 e 2 sono da definire in opera  | tenendo conto degli altri elementi a  | posizione vincolata: montanti del | parapetto, scalini, piastre, bulloni, | distanziatori...)
  TextSize = 3
  TextStyle = 0
  X = 282.79
  Y = 770.064
FEATURE [TechDraw::DrawViewAnnotation] Annotation016  label="dist_anno"
  Font = Arial
  KeepLabel = false
  LineSpace = 100
  MaxWidth = -1
  Rotation = 90
  ScaleType = 0
  Text = da definire in opera
  TextSize = 3
  TextStyle = 0
  X = 199.471
  Y = 471.708
FEATURE [Part::Part2DObjectPython] Rectangle002  # Draft 2D object (typed FeaturePython)
  ChamferSize = 0
  Columns = 1
  FilletRadius = 5
  Height = 100
  Length = 150
  MakeFace = false
  Placement = pos=(-110,-375,290) rot=(1,0,0;1.5708rad)
  Rows = 1
  Support = -> [Compound010]
FEATURE [Part::Part2DObjectPython] Rectangle003  # Draft 2D object (typed FeaturePython)
  ChamferSize = 0
  Columns = 1
  FilletRadius = 5
  Height = 100
  Length = 150
  MakeFace = false
  Placement = pos=(105,-375,290) rot=(1,0,0;1.5708rad)
  Rows = 1
FEATURE [App::DocumentObjectGroupPython] VisGroup  label="013_fridge_box_and_railing"  # scripted group (container) (typed FeaturePython)
  Group = -> [fridge_box_door_01_cs,DWire003,Line001,Line,Line002,Component007,Shape2DView,Rectangle002,Rectangle003]
FEATURE [App::DocumentObjectGroup] Group001  label="drawing"
  Group = -> [Compound007,VisGroup,VisGroup001,Compound008,Compound,Compound015,Rectangle]
FEATURE [TechDraw::DrawViewDraft] DraftView001  label="013_fridge_box001"
  Direction = (1,-100,0)
  FontSize = 12
  KeepLabel = false
  LineSpacing = 1
  LineStyle = Solid
  LineWidth = 0.1
  Rotation = 180
  Scale = 0.1
  ScaleType = 2
  Source = -> VisGroup
  Symbol = <blob: 16921 chars omitted>
  X = 28.8595
  Y = 323.676
  expr: Y = View.Y + 135.90000000000001
  expr: X = View.X - 175
FEATURE [TechDraw::DrawViewAnnotation] Annotation017  label="sagom_anno"
  Font = Arial
  KeepLabel = false
  LineSpace = 100
  MaxWidth = -1
  Rotation = 0
  ScaleType = 0
  Text = Prevedere la sagomatura della trave  | fissata al muro durante la fase di  | montaggio per consentire  | l'ispezionabilità delle cassette  | elettriche
  TextSize = 3
  TextStyle = 0
  X = 45.9788
  Y = 118.829
FEATURE [TechDraw::DrawPage] Page
  ProjectionType = 0
  Template = -> Template
  Views = -> [View,DraftView,DraftView001,DraftView002,Detail,Detail001,Detail002,View001,Detail003,DraftView003,Detail004,DraftView004,DraftView005,View002,Detail005,Detail006,Annotation,Annotation001,Annotation002,Annotation003,Annotation004,Annotation005,Annotation006,Annotation007,Annotation008,Annotation009,Annotation010,Dimension,Dimension001,Dimension002,Dimension003,Dimension004,Dimension005,+28 more]
